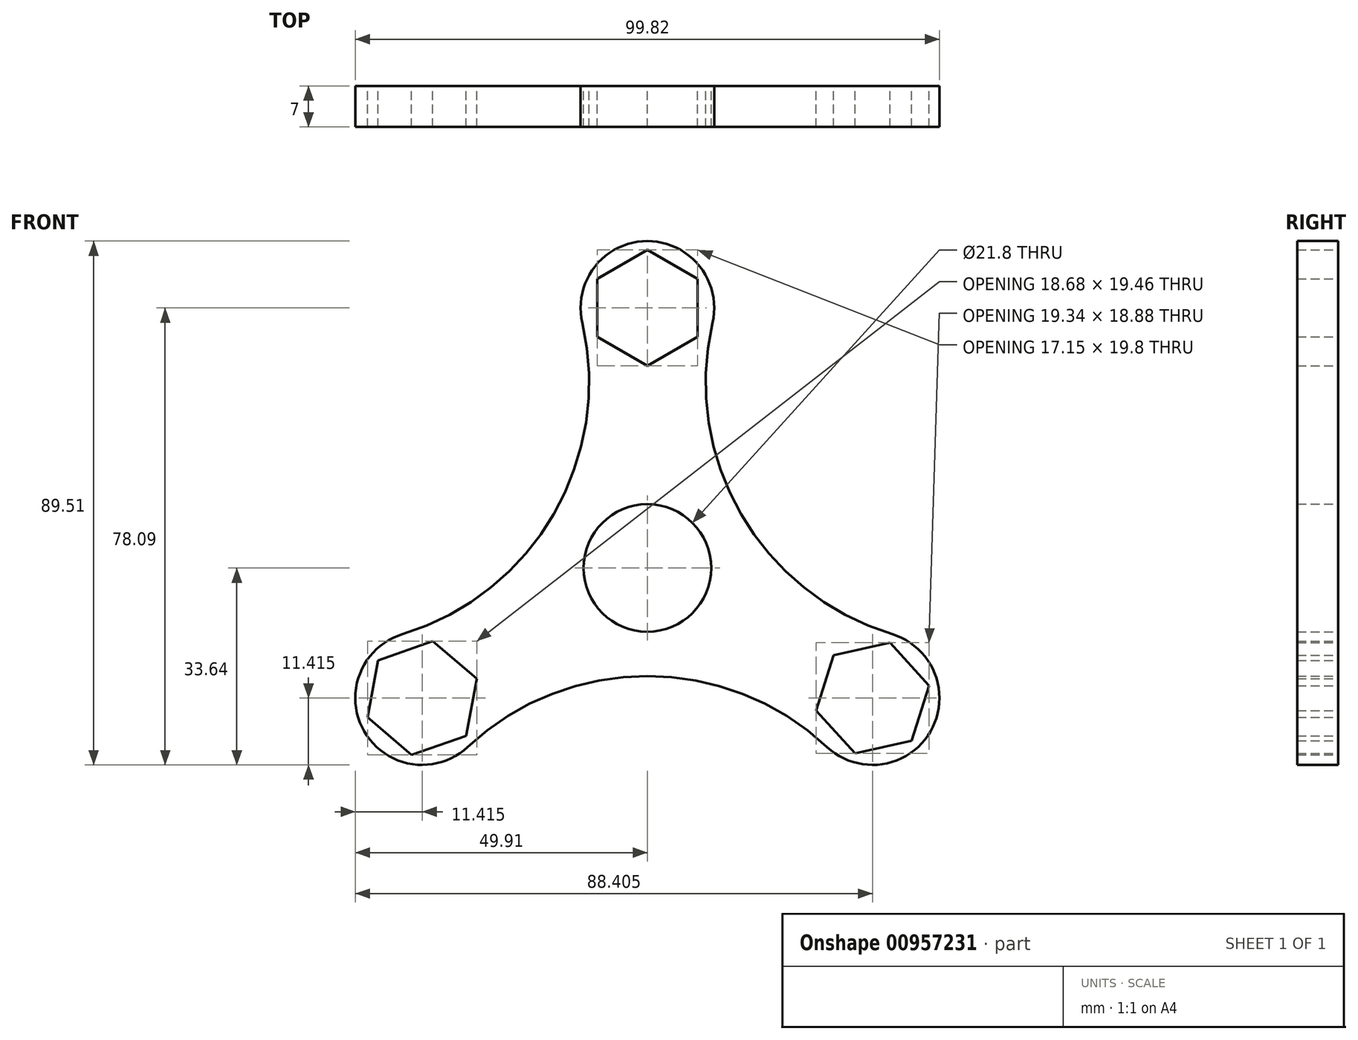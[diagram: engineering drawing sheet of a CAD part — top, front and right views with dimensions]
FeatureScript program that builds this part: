
annotation { "Feature Type Name" : "Feature", "Feature Type Description" : "" }
export const myFeature = defineFeature(function(context is Context, id is Id, definition is map)
    precondition{}
    {
        {
            var Q0;
            Q0=qCreatedBy(makeId("Front.planeOp"),FACE);
            var sketch = newSketch(context, id + "F0", { "sketchPlane" : qUnion([Q0])});
            skCircle(sketch, "E0", {"center": v(0, 0) * mm, "radius": 10.9 * mm});
            skArc(sketch, "E1", {"start": v(-42.06, -14.39) * mm, "mid": v(-42.05, -14.4) * mm, "end": v(-42.05, -14.42) * mm});
            skArc(sketch, "E2", {"start": v(11.13, 41.88) * mm, "mid": v(0, 55.87) * mm, "end": v(-11.13, 41.88) * mm});
            skArc(sketch, "E3.1.0", {"start": v(-41.83, -11.3) * mm, "mid": v(-48.38, -27.93) * mm, "end": v(-30.7, -30.57) * mm});
            skArc(sketch, "E3.2.0", {"start": v(30.7, -30.57) * mm, "mid": v(48.38, -27.93) * mm, "end": v(41.83, -11.3) * mm});
            skCircle(sketch, "E4.cCircle", {"center": v(0, 44.45) * mm, "radius": 8.57 * mm, "construction": true});
            skLineSegment(sketch, "E4.0", {"start": v(8.57, 49.4) * mm, "end": v(8.57, 39.5) * mm});
            skLineSegment(sketch, "E4.1", {"start": v(8.57, 39.5) * mm, "end": v(0, 34.55) * mm});
            skLineSegment(sketch, "E4.2", {"start": v(0, 34.55) * mm, "end": v(-8.57, 39.5) * mm});
            skLineSegment(sketch, "E4.3", {"start": v(-8.57, 39.5) * mm, "end": v(-8.57, 49.4) * mm});
            skLineSegment(sketch, "E4.4", {"start": v(-8.57, 49.4) * mm, "end": v(0, 54.35) * mm});
            skLineSegment(sketch, "E4.5", {"start": v(0, 54.35) * mm, "end": v(8.57, 49.4) * mm});
            skPoint(sketch, "E4.0.midPoint", {"position": v(8.57, 44.45) * mm});
            skCircle(sketch, "E5.cCircle", {"center": v(38.5, -22.22) * mm, "radius": 8.57 * mm, "construction": true});
            skLineSegment(sketch, "E5.0", {"start": v(48.16, -20.1) * mm, "end": v(45.18, -29.53) * mm});
            skLineSegment(sketch, "E5.1", {"start": v(45.18, -29.53) * mm, "end": v(35.5, -31.67) * mm});
            skLineSegment(sketch, "E5.2", {"start": v(35.5, -31.67) * mm, "end": v(28.83, -24.36) * mm});
            skLineSegment(sketch, "E5.3", {"start": v(28.83, -24.36) * mm, "end": v(31.81, -14.92) * mm});
            skLineSegment(sketch, "E5.4", {"start": v(31.81, -14.92) * mm, "end": v(41.48, -12.78) * mm});
            skLineSegment(sketch, "E5.5", {"start": v(41.48, -12.78) * mm, "end": v(48.16, -20.1) * mm});
            skPoint(sketch, "E5.0.midPoint", {"position": v(46.67, -24.81) * mm});
            skCircle(sketch, "E6.cCircle", {"center": v(-38.5, -22.22) * mm, "radius": 8.58 * mm, "construction": true});
            skLineSegment(sketch, "E6.0", {"start": v(-29.15, -18.94) * mm, "end": v(-30.98, -28.67) * mm});
            skLineSegment(sketch, "E6.1", {"start": v(-30.98, -28.67) * mm, "end": v(-40.32, -31.96) * mm});
            skLineSegment(sketch, "E6.2", {"start": v(-40.32, -31.96) * mm, "end": v(-47.84, -25.51) * mm});
            skLineSegment(sketch, "E6.3", {"start": v(-47.84, -25.51) * mm, "end": v(-46.01, -15.78) * mm});
            skLineSegment(sketch, "E6.4", {"start": v(-46.01, -15.78) * mm, "end": v(-36.67, -12.5) * mm});
            skLineSegment(sketch, "E6.5", {"start": v(-36.67, -12.5) * mm, "end": v(-29.15, -18.94) * mm});
            skPoint(sketch, "E6.0.midPoint", {"position": v(-30.07, -23.8) * mm});
            skArc(sketch, "E7", {"start": v(-41.83, -11.3) * mm, "mid": v(-16, 9.24) * mm, "end": v(-11.13, 41.88) * mm});
            skArc(sketch, "E8", {"start": v(11.13, 41.88) * mm, "mid": v(16, 9.24) * mm, "end": v(41.83, -11.3) * mm});
            skArc(sketch, "E9", {"start": v(30.7, -30.57) * mm, "mid": v(0, -18.47) * mm, "end": v(-30.7, -30.57) * mm});
            skArc(sketch, "E10.trimOffspring", {"start": v(8.57, 43.62) * mm, "mid": v(8.56, 43.62) * mm, "end": v(8.54, 43.62) * mm});
            skArc(sketch, "E11.trimOffspring", {"start": v(33.39, -29.35) * mm, "mid": v(33.45, -29.27) * mm, "end": v(33.51, -29.2) * mm});
            skArc(sketch, "E12.trimOffspring", {"start": v(-33.51, -29.2) * mm, "mid": v(-33.4, -29.34) * mm, "end": v(-33.27, -29.48) * mm});
            skArc(sketch, "E13.trimOffspring", {"start": v(42.05, -14.42) * mm, "mid": v(42.17, -14.05) * mm, "end": v(42.3, -13.67) * mm});
            skArc(sketch, "E14.trimOffspring", {"start": v(-8.54, 43.62) * mm, "mid": v(-8.56, 43.62) * mm, "end": v(-8.57, 43.62) * mm});
            skSolve(sketch);
        }
        {
            var Q0;
            Q0 = qSketchRegion(id + "F0", true);
            extrude(context, id + "F1", {"entities" : qUnion([Q0]), "depth" : 7 * mm, "offsetDistance" : 25 * mm});
        }
    });
